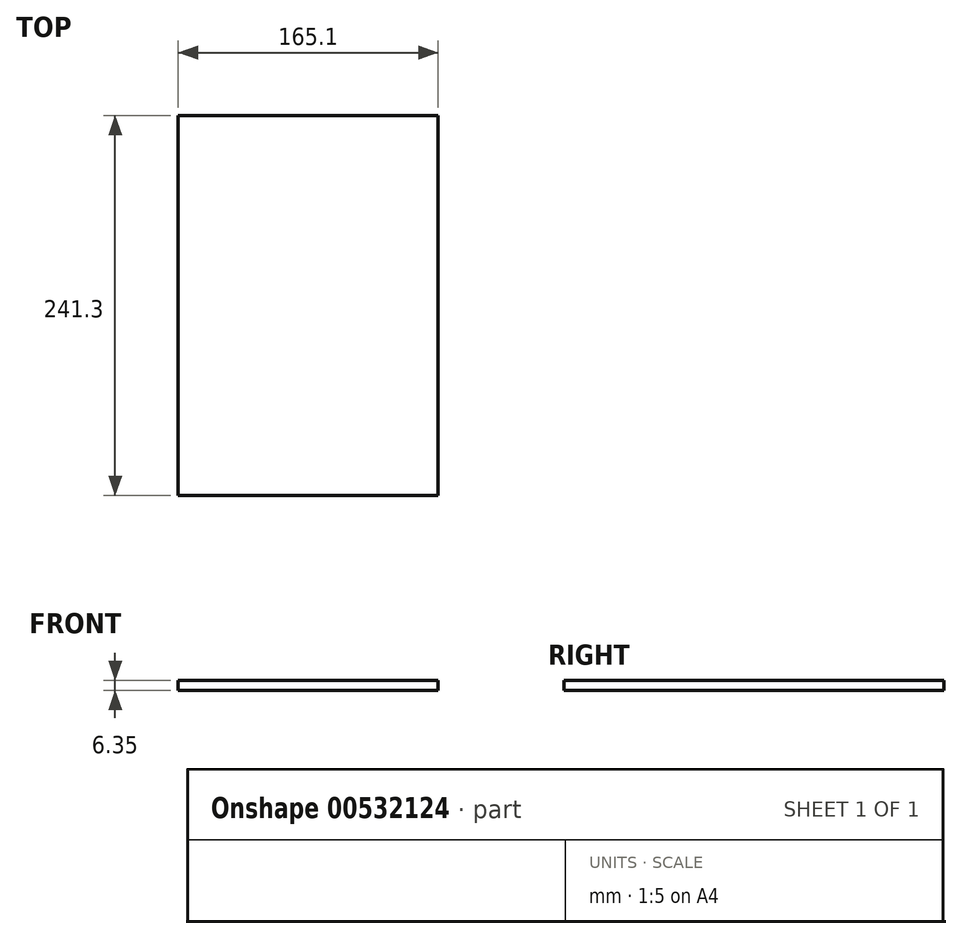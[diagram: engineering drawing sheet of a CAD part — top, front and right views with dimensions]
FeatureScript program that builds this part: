
annotation { "Feature Type Name" : "Feature", "Feature Type Description" : "" }
export const myFeature = defineFeature(function(context is Context, id is Id, definition is map)
    precondition{}
    {
        {
            var Q0;
            Q0=qCreatedBy(makeId("Top.planeOp"),FACE);
            var sketch = newSketch(context, id + "F0", { "sketchPlane" : qUnion([Q0])});
            skLineSegment(sketch, "E0.bottom", {"start": v(82.55, -120.65) * mm, "end": v(-82.55, -120.65) * mm});
            skLineSegment(sketch, "E0.top", {"start": v(82.55, 120.65) * mm, "end": v(-82.55, 120.65) * mm});
            skLineSegment(sketch, "E0.left", {"start": v(82.55, -120.65) * mm, "end": v(82.55, 120.65) * mm});
            skLineSegment(sketch, "E0.right", {"start": v(-82.55, -120.65) * mm, "end": v(-82.55, 120.65) * mm});
            skPoint(sketch, "E0.middle", {"position": v(0, 0) * mm});
            skSolve(sketch);
        }
        {
            var Q0;
            Q0=qSketchRegion(id+"F0",true);
            extrude(context, id + "F1", {"entities" : qUnion([Q0]), "depth" : 6.35 * mm, "offsetDistance" : 25.4 * mm});
        }
    });
